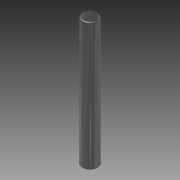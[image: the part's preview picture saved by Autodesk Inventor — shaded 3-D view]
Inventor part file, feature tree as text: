
AUTODESK INVENTOR PART (.ipt)
format: ipt  version: 2014 SP1 (Build 180222100, 222)  size: 85,504 bytes
history: native  units: in
note: dims shown in document units (in); Inventor stores cm internally (conversion verified against a paired STEP export)
features: revolve x1, sketch x1
ambient origin geometry x8: Origin, YZ Plane, XZ Plane, XY Plane, X Axis, Y Axis, Z Axis, Center Point
bodies: Solid1 (feature_tree)
feature tree (2):
  revolve  "Revolution1"  [1 undecoded]
  sketch  "Sketch1"  dims[d0=7.295in d2=0.77in d3=45.0deg d4=90.0deg d5=0.86in d6=0.125in d7=0.7in]
note: 1 required parameter value undecoded (feature->parameter linkage not recoverable at this tier; creation-order binding heuristic only, values carry confidence <= 0.55)
